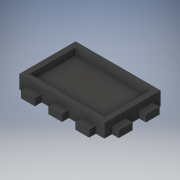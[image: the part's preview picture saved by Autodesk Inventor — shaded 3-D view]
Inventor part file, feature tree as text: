
AUTODESK INVENTOR PART (.ipt)
format: ipt  version: 2019 (Build 230136000, 136)  size: 202,752 bytes
history: native  units: mm
features: extrude x3, sketch x3, projected_geometry x2
ambient origin geometry x8: Origin, YZ Plane, XZ Plane, XY Plane, X Axis, Y Axis, Z Axis, Center Point
bodies: Solid1 (feature_tree)
feature tree (8):
  extrude  "Extrusion1"  Depth=41.0mm
  extrude  "Extrusion2"  Depth=4.0mm
  extrude  "Extrusion3"  Depth=4.0mm TaperAngle=0.0deg
  sketch  "Sketch1"  dims[d0=58.0mm d1=41.0mm]
  sketch  "Sketch2"  dims[d2=4.0mm d3=0.0mm d4=4.0mm]
  projected_geometry  "Projected Loop1"
  sketch  "Sketch3"  dims[d5=3.0mm d6=4.0mm d7=0.0mm d8=8.0mm d9=8.0mm d10=4.0mm d13=4.0mm d14=8.0mm d15=4.0mm d16=0.0mm]
  projected_geometry  "Projected Loop2"
